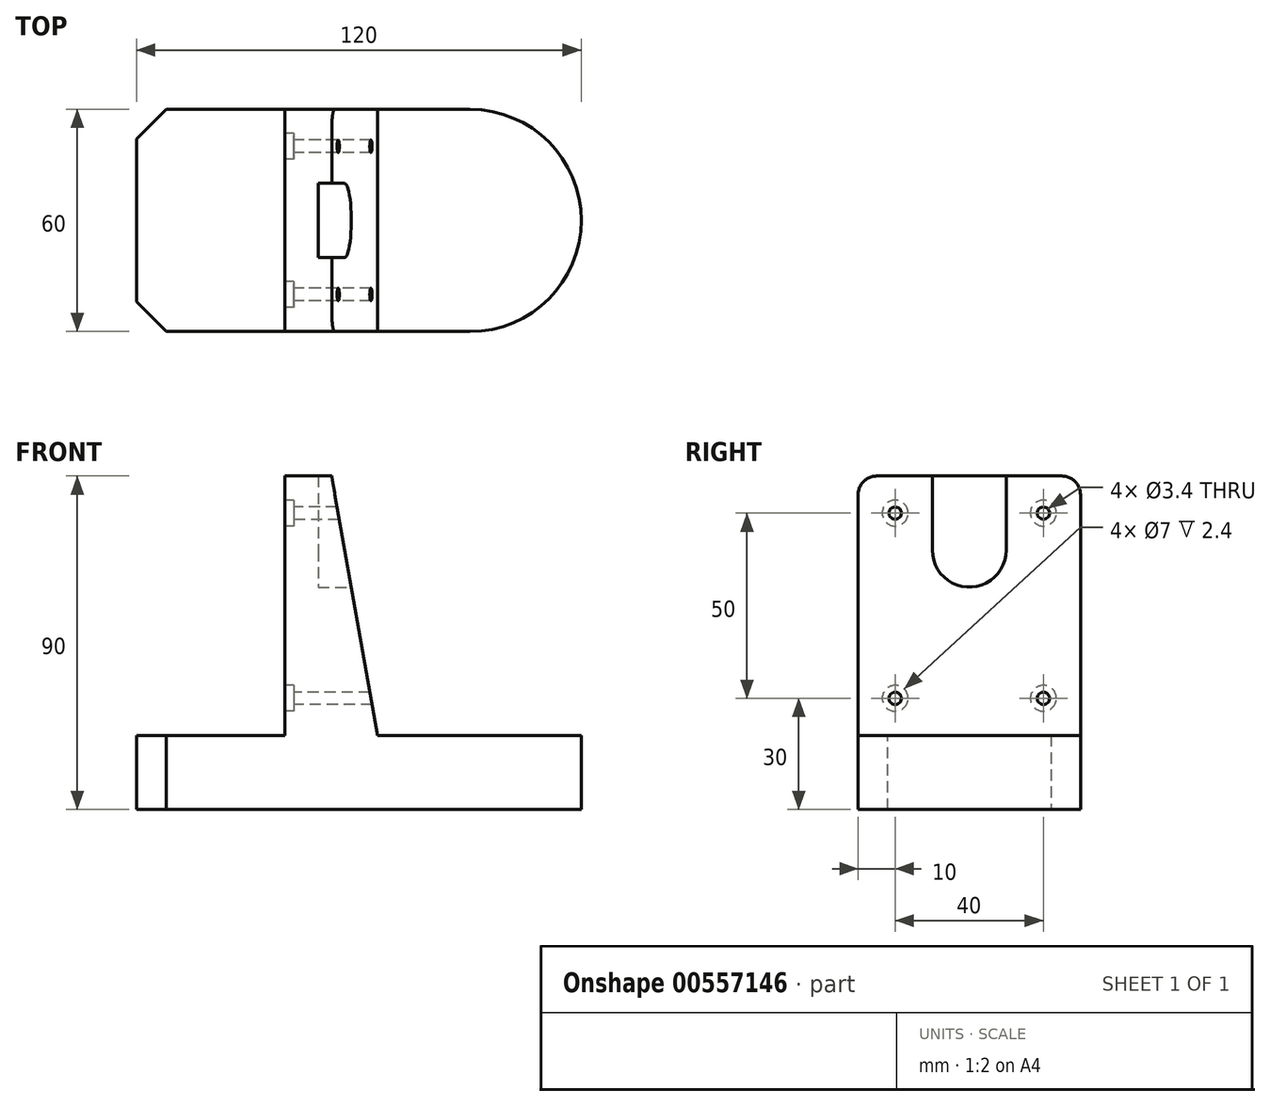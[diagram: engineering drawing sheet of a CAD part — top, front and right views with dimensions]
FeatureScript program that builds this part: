
annotation { "Feature Type Name" : "Feature", "Feature Type Description" : "" }
export const myFeature = defineFeature(function(context is Context, id is Id, definition is map)
    precondition{}
    {
        {
            var Q0;
            Q0=qCreatedBy(makeId("Top.planeOp"),FACE);
            var sketch = newSketch(context, id + "F0", { "sketchPlane" : qUnion([Q0])});
            skLineSegment(sketch, "E0.bottom", {"start": v(60, 30) * mm, "end": v(-60, 30) * mm});
            skLineSegment(sketch, "E0.top", {"start": v(60, -30) * mm, "end": v(-60, -30) * mm});
            skLineSegment(sketch, "E0.left", {"start": v(60, 30) * mm, "end": v(60, -30) * mm});
            skLineSegment(sketch, "E0.right", {"start": v(-60, 30) * mm, "end": v(-60, -30) * mm});
            skPoint(sketch, "E0.middle", {"position": v(0, 0) * mm});
            skSolve(sketch);
        }
        {
            var Q0;
            Q0 = qSketchRegion(id + "F0", true);
            extrude(context, id + "F1", {"entities" : qUnion([Q0]), "depth" : 90 * mm, "offsetDistance" : 25 * mm});
        }
        {
            var Q0;
            Q0=makeQuery(id+"F1.opExtrude","SWEPT_FACE",FACE,{"disambiguationData":[OSD([sQuery(id+"F0.wireOp",EDGE,"E0.top")])]});
            var sketch = newSketch(context, id + "F2", { "sketchPlane" : qUnion([Q0])});
            skLineSegment(sketch, "E1", {"start": v(-60, 20) * mm, "end": v(-20, 20) * mm});
            skLineSegment(sketch, "E2", {"start": v(-20, 20) * mm, "end": v(-20, 90) * mm});
            skLineSegment(sketch, "E3", {"start": v(-20, 90) * mm, "end": v(5, 90) * mm});
            skLineSegment(sketch, "E4", {"start": v(5, 90) * mm, "end": v(5, 20) * mm});
            skLineSegment(sketch, "E5", {"start": v(5, 20) * mm, "end": v(60, 20) * mm});
            skSolve(sketch);
        }
        {
            var Q0;
            {var subQ0=sQuery(id+"F2.wireOp",EDGE,"E1");Q0=makeQuery(id+"F2.imprint","IMPRINT",FACE,{"disambiguationData":[TD([[makeQuery(id+"F2.imprint","IMPRINT",EDGE,{"derivedFrom":subQ0}),1.0]])]});}
            var Q1;
            {var subQ0=sQuery(id+"F2.wireOp",EDGE,"E4");Q1=makeQuery(id+"F2.imprint","IMPRINT",FACE,{"disambiguationData":[TD([[makeQuery(id+"F2.imprint","IMPRINT",EDGE,{"derivedFrom":subQ0}),1.0]])]});}
            extrude(context, id + "F3", {"entities" : qUnion([Q0, Q1]), "operationType" : NewBodyOperationType.REMOVE, "endBound" : BoundingType.THROUGH_ALL, "oppositeDirection" : true, "depth" : 25 * mm, "offsetDistance" : 25 * mm});
        }
        {
            var Q0;
            Q0=makeQuery(id+"F1.opExtrude","SWEPT_EDGE",EDGE,{"disambiguationData":[OSD([sQuery(id+"F0.wireOp",EDGE,"E0.top"),sQuery(id+"F0.wireOp",EDGE,"E0.left")])]});
            var Q1;
            Q1=makeQuery(id+"F1.opExtrude","SWEPT_EDGE",EDGE,{"disambiguationData":[OSD([sQuery(id+"F0.wireOp",EDGE,"E0.bottom"),sQuery(id+"F0.wireOp",EDGE,"E0.left")])]});
            fillet(context, id + "F4", {"entities" : qUnion([Q0, Q1]), "radius" : 30 * mm, "tangentPropagation" : true, "allowEdgeOverflow" : false});
        }
        {
            var Q0;
            Q0=makeQuery(id+"F1.opExtrude","SWEPT_EDGE",EDGE,{"disambiguationData":[OSD([sQuery(id+"F0.wireOp",EDGE,"E0.top"),sQuery(id+"F0.wireOp",EDGE,"E0.right")])]});
            var Q1;
            Q1=makeQuery(id+"F1.opExtrude","SWEPT_EDGE",EDGE,{"disambiguationData":[OSD([sQuery(id+"F0.wireOp",EDGE,"E0.bottom"),sQuery(id+"F0.wireOp",EDGE,"E0.right")])]});
            chamfer(context, id + "F5", {"entities" : qUnion([Q0, Q1]), "width" : 8 * mm, "tangentPropagation" : true});
        }
        {
            var Q0;
            Q0=makeQuery(id+"F3.boolean.opBoolean","COPY",FACE,{"derivedFrom":makeQuery(id+"F3.opExtrude","SWEPT_FACE",FACE,{"disambiguationData":[OSD([sQuery(id+"F2.wireOp",EDGE,"E2")])]})});
            var sketch = newSketch(context, id + "F6", { "sketchPlane" : qUnion([Q0])});
            skPoint(sketch, "E6", {"position": v(-20, 80) * mm});
            skPoint(sketch, "E7", {"position": v(20, 80) * mm});
            skPoint(sketch, "E8", {"position": v(20, 30) * mm});
            skPoint(sketch, "E9", {"position": v(-20, 30) * mm});
            skSolve(sketch);
        }
        {
            var Q0;
            Q0=sQuery(id+"F6.wireOp",VERTEX,"E6");
            var Q1;
            Q1=sQuery(id+"F6.wireOp",VERTEX,"E7");
            var Q2;
            Q2=sQuery(id+"F6.wireOp",VERTEX,"E8");
            var Q3;
            Q3=sQuery(id+"F6.wireOp",VERTEX,"E9");
            var Q4;
            Q4=makeQuery(id+"F1.opExtrude","SWEPT_BODY",BODY,{"disambiguationData":[OSD([sQuery(id+"F0.wireOp",EDGE,"E0.bottom"),sQuery(id+"F0.wireOp",EDGE,"E0.top"),sQuery(id+"F0.wireOp",EDGE,"E0.left"),sQuery(id+"F0.wireOp",EDGE,"E0.right")])]});
            hole(context, id + "F7", {"style" : HoleStyle.C_BORE, "endStyle" : HoleEndStyle.THROUGH, "holeDiameter" : 3.4 * mm, "cBoreDiameter" : 7 * mm, "cBoreDepth" : 2.4 * mm, "isTappedThrough" : true, "tappedDepth" : 12 * mm, "tapClearance" : 3, "locations" : qUnion([Q0, Q1, Q2, Q3]), "scope" : qUnion([Q4])});
        }
        {
            var Q0;
            Q0=makeQuery(id+"F3.boolean.opBoolean","COPY",FACE,{"derivedFrom":makeQuery(id+"F3.opExtrude","SWEPT_FACE",FACE,{"disambiguationData":[OSD([sQuery(id+"F2.wireOp",EDGE,"E4")])]})});
            var sketch = newSketch(context, id + "F8", { "sketchPlane" : qUnion([Q0])});
            skLineSegment(sketch, "E10.bottom", {"start": v(-10, 90) * mm, "end": v(10, 90) * mm});
            skLineSegment(sketch, "E10.top", {"start": v(-10, 60) * mm, "end": v(10, 60) * mm});
            skLineSegment(sketch, "E10.left", {"start": v(-10, 90) * mm, "end": v(-10, 60) * mm});
            skLineSegment(sketch, "E10.right", {"start": v(10, 90) * mm, "end": v(10, 60) * mm});
            skCircle(sketch, "E11", {"center": v(0, 70) * mm, "radius": 10 * mm});
            skSolve(sketch);
        }
        {
            var Q0;
            {var subQ0=sQuery(id+"F8.wireOp",EDGE,"E11");var subQ1=makeQuery(id+"F8.imprint","INTERSECT",VERTEX,{"derivedFrom":[sQuery(id+"F8.wireOp",EDGE,"E10.left"),subQ0]});Q0=makeQuery(id+"F8.imprint","IMPRINT",FACE,{"disambiguationData":[TD([[makeQuery(id+"F8.imprint","IMPRINT",EDGE,{"disambiguationData":[TD([[subQ1,1.0]])],"derivedFrom":subQ0}),1.0]])]});}
            var Q1;
            {var subQ0=sQuery(id+"F8.wireOp",EDGE,"E10.bottom");Q1=makeQuery(id+"F8.imprint","IMPRINT",FACE,{"disambiguationData":[TD([[makeQuery(id+"F8.imprint","IMPRINT",EDGE,{"derivedFrom":subQ0}),1.0]])]});}
            extrude(context, id + "F9", {"entities" : qUnion([Q0, Q1]), "operationType" : NewBodyOperationType.REMOVE, "oppositeDirection" : true, "depth" : 16 * mm, "offsetDistance" : 25 * mm});
        }
        {
            var Q0;
            Q0=makeQuery(id+"F1.opExtrude","SWEPT_FACE",FACE,{"disambiguationData":[OSD([sQuery(id+"F0.wireOp",EDGE,"E0.top")])]});
            var sketch = newSketch(context, id + "F10", { "sketchPlane" : qUnion([Q0])});
            skLineSegment(sketch, "E12", {"start": v(-7.34, 90) * mm, "end": v(5, 20) * mm});
            skSolve(sketch);
        }
        {
            var Q0;
            {var subQ0=sQuery(id+"F10.wireOp",EDGE,"E12");Q0=makeQuery(id+"F10.imprint","IMPRINT",FACE,{"disambiguationData":[TD([[makeQuery(id+"F10.imprint","IMPRINT",EDGE,{"derivedFrom":subQ0}),1.0]])]});}
            extrude(context, id + "F11", {"entities" : qUnion([Q0]), "operationType" : NewBodyOperationType.REMOVE, "endBound" : BoundingType.THROUGH_ALL, "oppositeDirection" : true, "depth" : 25 * mm, "offsetDistance" : 25 * mm});
        }
        {
            var Q0;
            Q0=makeQuery(id+"F1.opExtrude","CAP_EDGE",EDGE,{"disambiguationData":[OSD([sQuery(id+"F0.wireOp",EDGE,"E0.top")])],"isStart":false});
            var Q1;
            Q1=makeQuery(id+"F1.opExtrude","CAP_EDGE",EDGE,{"disambiguationData":[OSD([sQuery(id+"F0.wireOp",EDGE,"E0.bottom")])],"isStart":false});
            fillet(context, id + "F12", {"entities" : qUnion([Q0, Q1]), "radius" : 5 * mm, "tangentPropagation" : true, "allowEdgeOverflow" : false});
        }
    });
